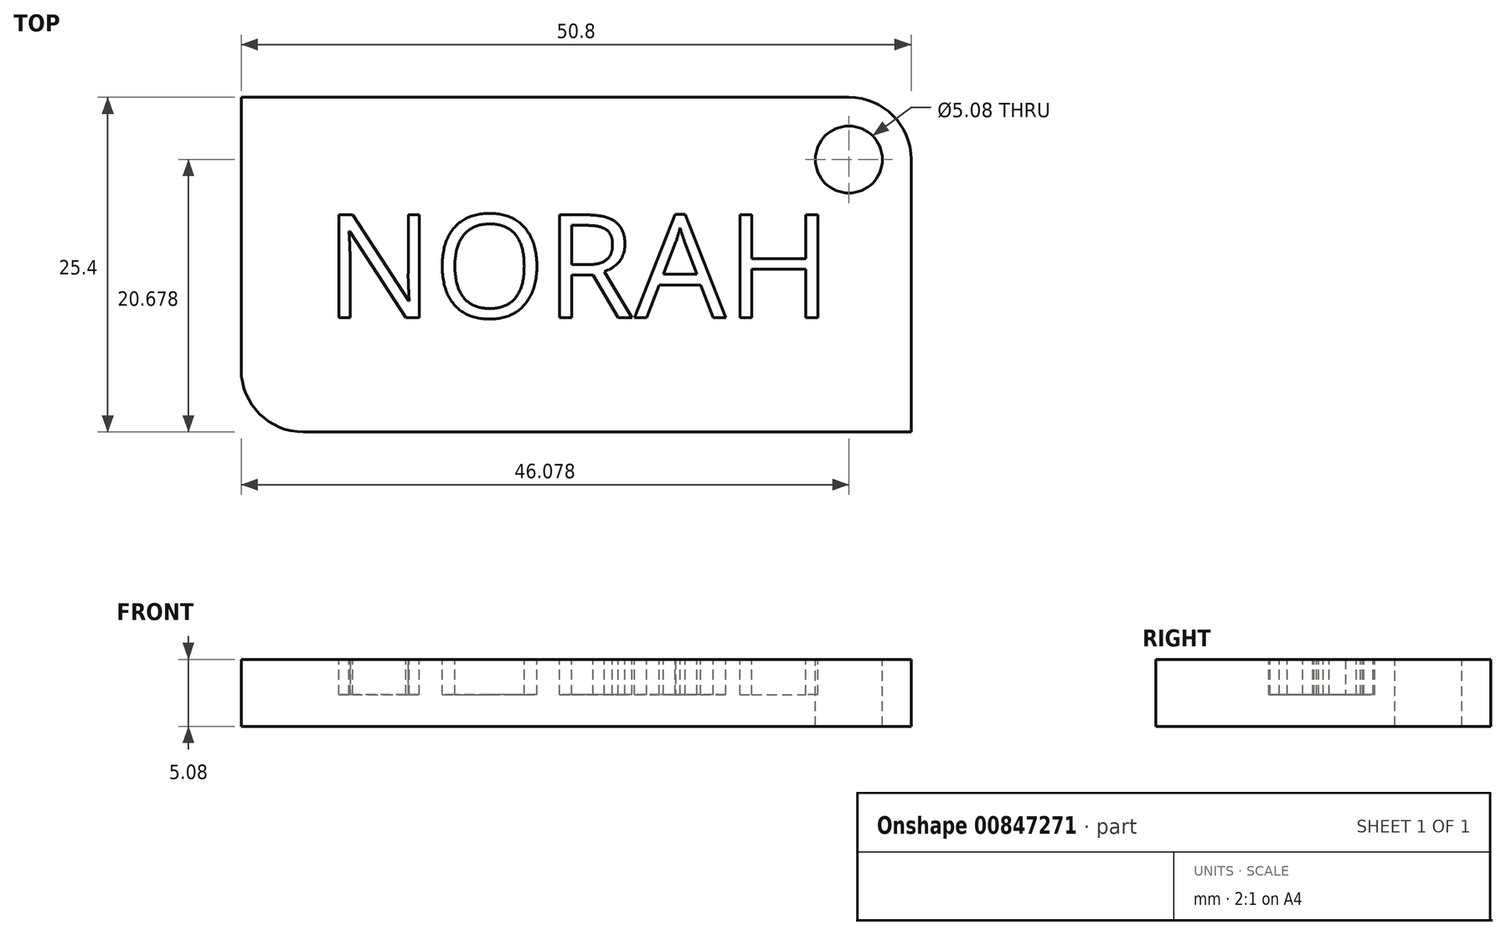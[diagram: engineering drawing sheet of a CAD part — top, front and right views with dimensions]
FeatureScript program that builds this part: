
annotation { "Feature Type Name" : "Feature", "Feature Type Description" : "" }
export const myFeature = defineFeature(function(context is Context, id is Id, definition is map)
    precondition{}
    {
        {
            var Q0;
            Q0=qCreatedBy(makeId("Top.planeOp"),FACE);
            var sketch = newSketch(context, id + "F0", { "sketchPlane" : qUnion([Q0])});
            skLineSegment(sketch, "E0.bottom", {"start": v(25.4, -12.7) * mm, "end": v(-25.4, -12.7) * mm});
            skLineSegment(sketch, "E0.top", {"start": v(25.4, 12.7) * mm, "end": v(-25.4, 12.7) * mm});
            skLineSegment(sketch, "E0.left", {"start": v(25.4, -12.7) * mm, "end": v(25.4, 12.7) * mm});
            skLineSegment(sketch, "E0.right", {"start": v(-25.4, -12.7) * mm, "end": v(-25.4, 12.7) * mm});
            skPoint(sketch, "E0.middle", {"position": v(0, 0) * mm});
            skSolve(sketch);
        }
        {
            var Q0;
            Q0=makeQuery(id+"F0.imprint","IMPRINT",FACE,{"disambiguationData":[TD([[makeQuery(id+"F0.imprint","IMPRINT",EDGE,{"derivedFrom":sQuery(id+"F0.wireOp",EDGE,"E0.bottom")}),-1.0]])]});
            extrude(context, id + "F1", {"entities" : qUnion([Q0]), "depth" : 5.08 * mm, "offsetDistance" : 25.4 * mm});
        }
        {
            var Q0;
            Q0=makeQuery(id+"F1.opExtrude","CAP_FACE",FACE,{"disambiguationData":[OSD([sQuery(id+"F0.wireOp",EDGE,"E0.bottom"),sQuery(id+"F0.wireOp",EDGE,"E0.top"),sQuery(id+"F0.wireOp",EDGE,"E0.left"),sQuery(id+"F0.wireOp",EDGE,"E0.right")])],"isStart":false});
            var sketch = newSketch(context, id + "F2", { "sketchPlane" : qUnion([Q0])});
            skText(sketch, "E1", { "text": "NORAH", "fontName": "OpenSans-Regular.ttf"});
            skLineSegment(sketch, "E2", {"start": v(-19.05, 0) * mm, "end": v(19.05, 0) * mm, "construction": true});
            skPoint(sketch, "E2.startSnap0", {"position": v(-25.4, 0) * mm});
            skPoint(sketch, "E2.endSnap0", {"position": v(-25.4, 0) * mm});
            skPoint(sketch, "E3", {"position": v(0, 0) * mm});
            const initialGuessF2  = {"E1": [-0.01905, -0.00402, 1, 0, 0.00786]};
            skSetInitialGuess(sketch, initialGuessF2);
            skSolve(sketch);
        }
        {
            var Q0;
            Q0 = qSketchRegion(id + "F2", true);
            extrude(context, id + "F3", {"entities" : qUnion([Q0]), "operationType" : NewBodyOperationType.REMOVE, "oppositeDirection" : true, "depth" : 2.7 * mm, "offsetDistance" : 25.4 * mm});
        }
        {
            var Q0;
            Q0=makeQuery(id+"F1.opExtrude","SWEPT_EDGE",EDGE,{"disambiguationData":[OSD([sQuery(id+"F0.wireOp",EDGE,"E0.top"),sQuery(id+"F0.wireOp",EDGE,"E0.left")])]});
            var Q1;
            Q1=makeQuery(id+"F1.opExtrude","SWEPT_EDGE",EDGE,{"disambiguationData":[OSD([sQuery(id+"F0.wireOp",EDGE,"E0.bottom"),sQuery(id+"F0.wireOp",EDGE,"E0.right")])]});
            fillet(context, id + "F4", {"entities" : qUnion([Q0, Q1]), "radius" : 4.72 * mm, "tangentPropagation" : true, "allowEdgeOverflow" : false});
        }
        {
            var Q0;
            {var subQ0=sQuery(id+"F0.wireOp",EDGE,"E0.left");var subQ1=sQuery(id+"F0.wireOp",EDGE,"E0.bottom");var subQ2=sQuery(id+"F0.wireOp",EDGE,"E0.right");var subQ3=sQuery(id+"F0.wireOp",EDGE,"E0.top");Q0=makeQuery(id+"F3.boolean.opBoolean","SPLIT",FACE,{"disambiguationData":[TD([makeQuery(id+"F1.opExtrude","SWEPT_FACE",FACE,{"disambiguationData":[OSD([subQ1])]})])],"derivedFrom":makeQuery(id+"F1.opExtrude","CAP_FACE",FACE,{"disambiguationData":[OSD([subQ1,subQ3,subQ0,subQ2])],"isStart":false})});}
            var sketch = newSketch(context, id + "F5", { "sketchPlane" : qUnion([Q0])});
            skCircle(sketch, "E4", {"center": v(20.68, 7.98) * mm, "radius": 2.54 * mm});
            skSolve(sketch);
        }
        {
            var Q0;
            Q0=makeQuery(id+"F5.imprint","IMPRINT",FACE,{"disambiguationData":[TD([[makeQuery(id+"F5.imprint","IMPRINT",EDGE,{"derivedFrom":sQuery(id+"F5.wireOp",EDGE,"E4")}),1.0]])]});
            extrude(context, id + "F6", {"entities" : qUnion([Q0]), "operationType" : NewBodyOperationType.REMOVE, "endBound" : BoundingType.THROUGH_ALL, "oppositeDirection" : true, "depth" : 25.4 * mm, "offsetDistance" : 25.4 * mm});
        }
    });
